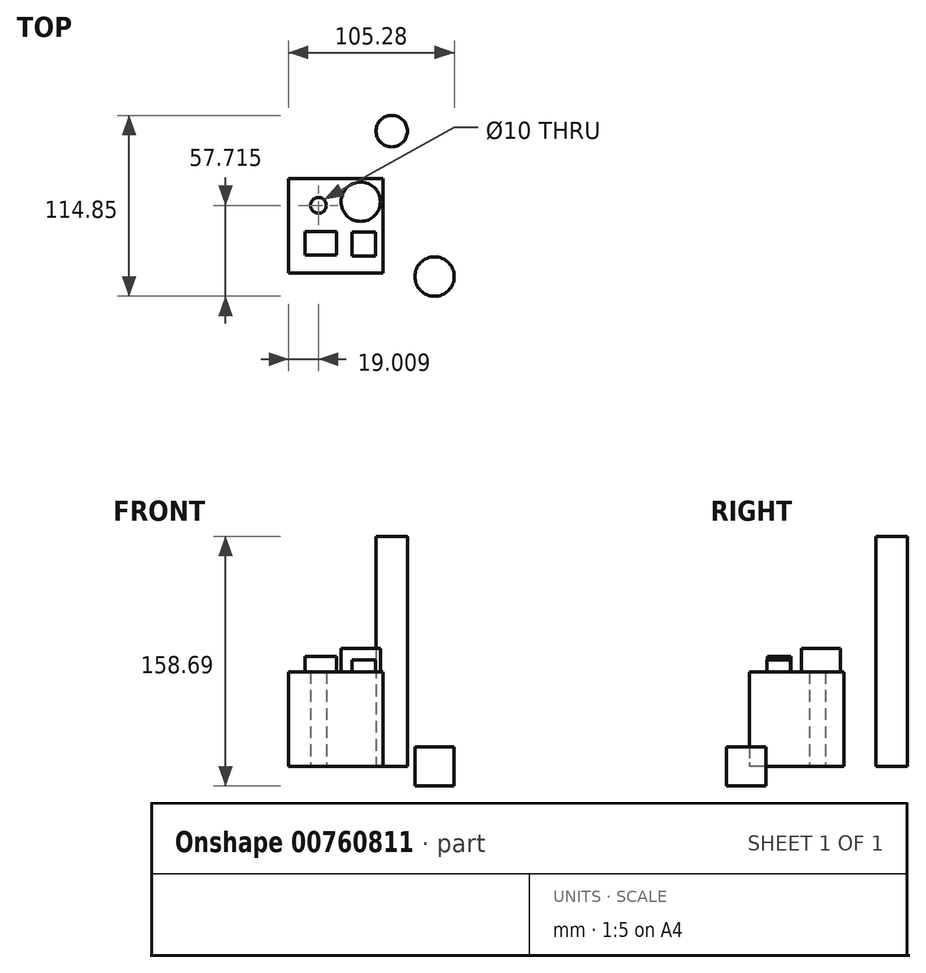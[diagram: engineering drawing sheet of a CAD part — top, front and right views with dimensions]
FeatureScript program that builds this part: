
annotation { "Feature Type Name" : "Feature", "Feature Type Description" : "" }
export const myFeature = defineFeature(function(context is Context, id is Id, definition is map)
    precondition{}
    {
        {
            var Q0;
            Q0=qCreatedBy(makeId("Top.planeOp"),FACE);
            var sketch = newSketch(context, id + "F0", { "sketchPlane" : qUnion([Q0])});
            skLineSegment(sketch, "E0.bottom", {"start": v(-38.84, 28.95) * mm, "end": v(21.16, 28.95) * mm});
            skLineSegment(sketch, "E0.top", {"start": v(-38.84, -31.05) * mm, "end": v(21.16, -31.05) * mm});
            skLineSegment(sketch, "E0.left", {"start": v(-38.84, 28.95) * mm, "end": v(-38.84, -31.05) * mm});
            skLineSegment(sketch, "E0.right", {"start": v(21.16, 28.95) * mm, "end": v(21.16, -31.05) * mm});
            skCircle(sketch, "E1", {"center": v(-19.83, 11.98) * mm, "radius": 5 * mm});
            skSolve(sketch);
        }
        {
            var Q0;
            Q0=makeQuery(id+"F0.imprint","IMPRINT",FACE,{"disambiguationData":[TD([[makeQuery(id+"F0.imprint","IMPRINT",EDGE,{"derivedFrom":sQuery(id+"F0.wireOp",EDGE,"E0.bottom")}),-1.0]])]});
            extrude(context, id + "F1", {"entities" : qUnion([Q0]), "depth" : 60 * mm, "offsetDistance" : 25 * mm});
        }
        {
            var Q0;
            Q0 = qSketchRegion(id + "F0", true);
            extrude(context, id + "F2", {"entities" : qUnion([Q0]), "operationType" : NewBodyOperationType.ADD, "depth" : 25 * mm, "offsetDistance" : 25 * mm});
        }
        {
            var Q0;
            Q0=makeQuery(id+"F1.opExtrude","CAP_FACE",FACE,{"disambiguationData":[OSD([sQuery(id+"F0.wireOp",EDGE,"E0.bottom"),sQuery(id+"F0.wireOp",EDGE,"E0.top"),sQuery(id+"F0.wireOp",EDGE,"E0.left"),sQuery(id+"F0.wireOp",EDGE,"E0.right"),sQuery(id+"F0.wireOp",EDGE,"E1")])],"isStart":false});
            var sketch = newSketch(context, id + "F3", { "sketchPlane" : qUnion([Q0])});
            skLineSegment(sketch, "E2.bottom", {"start": v(-28.4, -4.72) * mm, "end": v(-8.4, -4.72) * mm});
            skLineSegment(sketch, "E2.top", {"start": v(-28.4, -19.72) * mm, "end": v(-8.4, -19.72) * mm});
            skLineSegment(sketch, "E2.left", {"start": v(-28.4, -4.72) * mm, "end": v(-28.4, -19.72) * mm});
            skLineSegment(sketch, "E2.right", {"start": v(-8.4, -4.72) * mm, "end": v(-8.4, -19.72) * mm});
            skSolve(sketch);
        }
        {
            var Q0;
            Q0=makeQuery(id+"F3.imprint","IMPRINT",FACE,{"disambiguationData":[TD([[makeQuery(id+"F3.imprint","IMPRINT",EDGE,{"derivedFrom":sQuery(id+"F3.wireOp",EDGE,"E2.bottom")}),-1.0]])]});
            extrude(context, id + "F4", {"entities" : qUnion([Q0]), "operationType" : NewBodyOperationType.ADD, "depth" : 10 * mm, "offsetDistance" : 25 * mm});
        }
        {
            var Q0;
            Q0=makeQuery(id+"F1.opExtrude","CAP_FACE",FACE,{"disambiguationData":[OSD([sQuery(id+"F0.wireOp",EDGE,"E0.bottom"),sQuery(id+"F0.wireOp",EDGE,"E0.top"),sQuery(id+"F0.wireOp",EDGE,"E0.left"),sQuery(id+"F0.wireOp",EDGE,"E0.right"),sQuery(id+"F0.wireOp",EDGE,"E1")])],"isStart":false});
            var sketch = newSketch(context, id + "F5", { "sketchPlane" : qUnion([Q0])});
            skLineSegment(sketch, "E3.bottom", {"start": v(1.5, -5.15) * mm, "end": v(16.5, -5.15) * mm});
            skLineSegment(sketch, "E3.top", {"start": v(1.5, -20.15) * mm, "end": v(16.5, -20.15) * mm});
            skLineSegment(sketch, "E3.left", {"start": v(1.5, -5.15) * mm, "end": v(1.5, -20.15) * mm});
            skLineSegment(sketch, "E3.right", {"start": v(16.5, -5.15) * mm, "end": v(16.5, -20.15) * mm});
            skSolve(sketch);
        }
        {
            var Q0;
            Q0=makeQuery(id+"F5.imprint","IMPRINT",FACE,{"disambiguationData":[TD([[makeQuery(id+"F5.imprint","IMPRINT",EDGE,{"derivedFrom":sQuery(id+"F5.wireOp",EDGE,"E3.bottom")}),-1.0]])]});
            extrude(context, id + "F6", {"entities" : qUnion([Q0]), "operationType" : NewBodyOperationType.ADD, "depth" : 7.5 * mm, "offsetDistance" : 25 * mm});
        }
        {
            var Q0;
            Q0=makeQuery(id+"F1.opExtrude","CAP_FACE",FACE,{"disambiguationData":[OSD([sQuery(id+"F0.wireOp",EDGE,"E0.bottom"),sQuery(id+"F0.wireOp",EDGE,"E0.top"),sQuery(id+"F0.wireOp",EDGE,"E0.left"),sQuery(id+"F0.wireOp",EDGE,"E0.right"),sQuery(id+"F0.wireOp",EDGE,"E1")])],"isStart":false});
            var sketch = newSketch(context, id + "F7", { "sketchPlane" : qUnion([Q0])});
            skCircle(sketch, "E4", {"center": v(7, 14.27) * mm, "radius": 12.5 * mm});
            skSolve(sketch);
        }
        {
            var Q0;
            Q0=makeQuery(id+"F7.imprint","IMPRINT",FACE,{"disambiguationData":[TD([[makeQuery(id+"F7.imprint","IMPRINT",EDGE,{"derivedFrom":sQuery(id+"F7.wireOp",EDGE,"E4")}),1.0]])]});
            extrude(context, id + "F8", {"entities" : qUnion([Q0]), "operationType" : NewBodyOperationType.ADD, "depth" : 15 * mm, "offsetDistance" : 25 * mm});
        }
        {
            var Q0;
            Q0=qCreatedBy(makeId("Top.planeOp"),FACE);
            var sketch = newSketch(context, id + "F9", { "sketchPlane" : qUnion([Q0])});
            skCircle(sketch, "E5", {"center": v(26.73, 59.11) * mm, "radius": 10 * mm});
            skSolve(sketch);
        }
        {
            var Q0;
            Q0=makeQuery(id+"F9.imprint","IMPRINT",FACE,{"disambiguationData":[TD([[makeQuery(id+"F9.imprint","IMPRINT",EDGE,{"derivedFrom":sQuery(id+"F9.wireOp",EDGE,"E5")}),1.0]])]});
            extrude(context, id + "F10", {"entities" : qUnion([Q0]), "endBound" : BoundingType.THROUGH_ALL, "depth" : 25 * mm, "offsetDistance" : 25 * mm});
        }
        {
            var Q0;
            Q0=qCreatedBy(makeId("Top.planeOp"),FACE);
            var sketch = newSketch(context, id + "F11", { "sketchPlane" : qUnion([Q0])});
            skCircle(sketch, "E6", {"center": v(53.94, -33.24) * mm, "radius": 12.5 * mm});
            skSolve(sketch);
        }
        {
            var Q0;
            Q0=makeQuery(id+"F11.imprint","IMPRINT",FACE,{"disambiguationData":[TD([[makeQuery(id+"F11.imprint","IMPRINT",EDGE,{"derivedFrom":sQuery(id+"F11.wireOp",EDGE,"E6")}),1.0]])]});
            extrude(context, id + "F12", {"entities" : qUnion([Q0]), "endBound" : BoundingType.SYMMETRIC, "depth" : 25 * mm, "offsetDistance" : 25 * mm});
        }
    });
